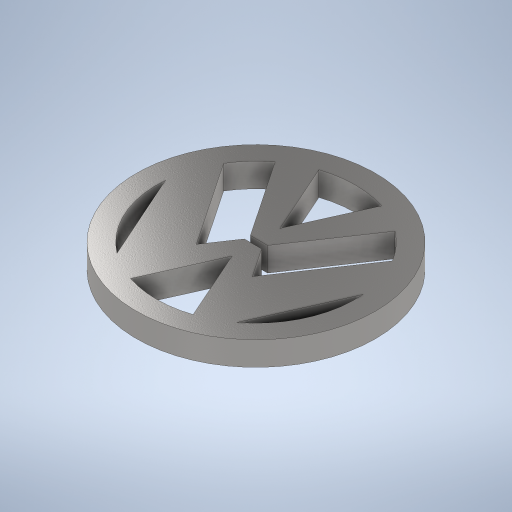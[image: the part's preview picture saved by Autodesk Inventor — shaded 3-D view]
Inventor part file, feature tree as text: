
AUTODESK INVENTOR PART (.ipt)
format: ipt  version: 2024 (Build 280153000, 153)  size: 345,088 bytes
history: native  units: mm
features: extrude x4, sketch x4, pattern_circular x1, plane x1, mirror x1
ambient origin geometry x8: Origin, YZ Plane, XZ Plane, XY Plane, X Axis, Y Axis, Z Axis, Center Point
bodies: Body1 (feature_tree), Body2 (feature_tree)
feature tree (11):
  extrude  "Extrusion3"  Depth=83.0mm
  extrude  "Extrusion4"  Depth=10.0mm
  pattern_circular  "Runde Anordnung1"  Count=2 Angle=360.0deg
  extrude  "Extrusion5"  Depth=2.5mm
  extrude  "Extrusion6"  Depth=10.0mm
  plane  "Arbeitsebene1"
  mirror  "Spiegeln1"
  sketch  "Skizze2"  dims[d12=100.0mm d13=83.0mm]
  sketch  "Skizze3"  dims[d14=10.0mm d15=0.0mm d16=8.37758mm]
  sketch  "Skizze4"  dims[d17=10.0mm]
  sketch  "Skizze5"  dims[d18=10.0mm d19=0.0mm d20=20.0mm d21=360.0deg d23=2.5mm d30=12.0mm d31=1.745329mm d32=1.745329mm d33=1.745329mm d34=1.745329mm d35=10.0mm d36=0.0mm d41=1.745329mm d42=10.0mm d43=0.0mm d44=0.0mm]
